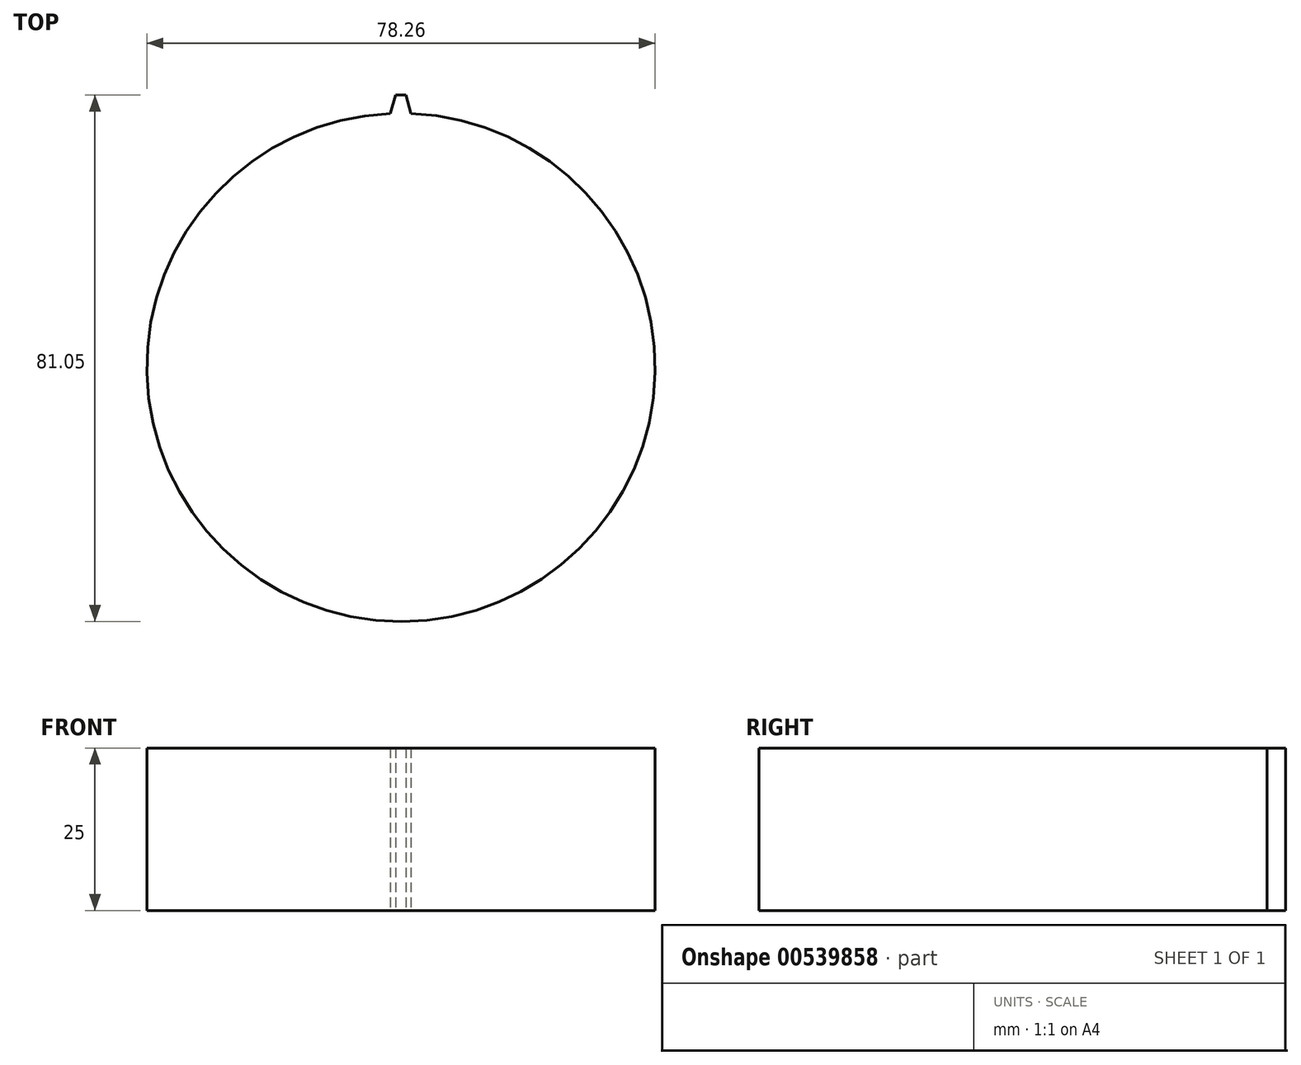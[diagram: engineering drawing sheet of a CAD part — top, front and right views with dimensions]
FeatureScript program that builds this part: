
annotation { "Feature Type Name" : "Feature", "Feature Type Description" : "" }
export const myFeature = defineFeature(function(context is Context, id is Id, definition is map)
    precondition{}
    {
        {
            var Q0;
            Q0=qCreatedBy(makeId("Top.planeOp"),FACE);
            var sketch = newSketch(context, id + "F0", { "sketchPlane" : qUnion([Q0])});
            skCircle(sketch, "E0", {"center": v(0, 0) * mm, "radius": 39.13 * mm});
            skLineSegment(sketch, "E1", {"start": v(-1.63, 39.1) * mm, "end": v(-0.86, 41.92) * mm});
            skLineSegment(sketch, "E2", {"start": v(-0.86, 41.92) * mm, "end": v(0.75, 41.92) * mm});
            skLineSegment(sketch, "E3", {"start": v(0.75, 41.92) * mm, "end": v(1.53, 39.1) * mm});
            skLineSegment(sketch, "E4", {"start": v(1.53, 39.1) * mm, "end": v(-1.63, 39.1) * mm});
            skSolve(sketch);
        }
        {
            var Q0;
            Q0 = qSketchRegion(id + "F0", true);
            extrude(context, id + "F1", {"entities" : qUnion([Q0]), "depth" : 25 * mm, "offsetDistance" : 25 * mm});
        }
    });
